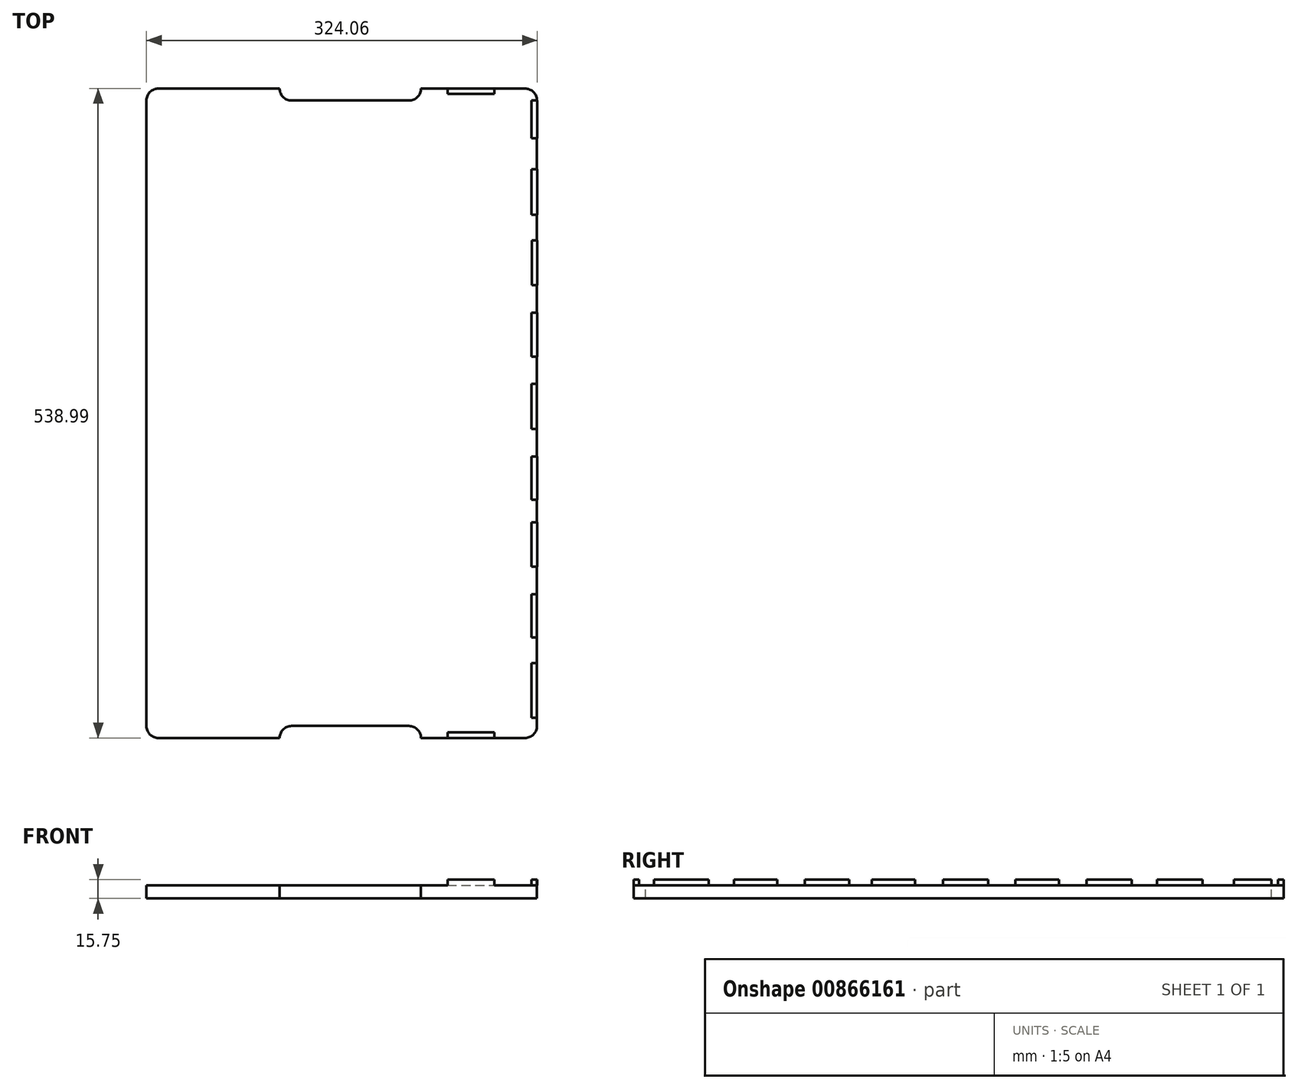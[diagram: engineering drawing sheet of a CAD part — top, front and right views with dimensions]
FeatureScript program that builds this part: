
annotation { "Feature Type Name" : "Feature", "Feature Type Description" : "" }
export const myFeature = defineFeature(function(context is Context, id is Id, definition is map)
    precondition{}
    {
        {
            var Q0;
            Q0=qCreatedBy(makeId("Top.planeOp"),FACE);
            var sketch = newSketch(context, id + "F0", { "sketchPlane" : qUnion([Q0])});
            skLineSegment(sketch, "E0.bottom", {"start": v(-151.16, 267.27) * mm, "end": v(-50.64, 267.27) * mm});
            skLineSegment(sketch, "E0.top", {"start": v(-151.16, -271.72) * mm, "end": v(152.88, -271.72) * mm});
            skLineSegment(sketch, "E0.left", {"start": v(-161.06, 257.36) * mm, "end": v(-161.06, -261.81) * mm});
            skLineSegment(sketch, "E0.right", {"start": v(162.79, 257.36) * mm, "end": v(162.79, -261.81) * mm});
            skPoint(sketch, "E1.visualSharp", {"position": v(-161.06, 267.27) * mm});
            skArc(sketch, "E1.filletArc", {"start": v(-151.16, 267.27) * mm, "mid": v(-158.16, 264.37) * mm, "end": v(-161.06, 257.36) * mm});
            skPoint(sketch, "E2.visualSharp", {"position": v(162.79, 267.27) * mm});
            skArc(sketch, "E2.filletArc", {"start": v(162.79, 257.36) * mm, "mid": v(159.89, 264.37) * mm, "end": v(152.88, 267.27) * mm});
            skPoint(sketch, "E3.visualSharp", {"position": v(162.79, -271.72) * mm});
            skArc(sketch, "E3.filletArc", {"start": v(152.88, -271.72) * mm, "mid": v(159.89, -268.82) * mm, "end": v(162.79, -261.81) * mm});
            skPoint(sketch, "E4.visualSharp", {"position": v(-161.06, -271.72) * mm});
            skArc(sketch, "E4.filletArc", {"start": v(-161.06, -261.81) * mm, "mid": v(-158.16, -268.82) * mm, "end": v(-151.16, -271.72) * mm});
            skPoint(sketch, "E5", {"position": v(-51.16, 267.27) * mm});
            skPoint(sketch, "E6", {"position": v(-41.25, 267.27) * mm});
            skPoint(sketch, "E7", {"position": v(66.6, 267.27) * mm});
            skPoint(sketch, "E8", {"position": v(56.7, 267.27) * mm});
            skLineSegment(sketch, "E9", {"start": v(-40.81, 267.27) * mm, "end": v(56.04, 267.27) * mm});
            skLineSegment(sketch, "E10", {"start": v(56.04, 267.27) * mm, "end": v(56.7, 267.27) * mm});
            skLineSegment(sketch, "E11", {"start": v(-41.25, 267.27) * mm, "end": v(-40.81, 267.27) * mm});
            skLineSegment(sketch, "E12.trimOffspring", {"start": v(66.6, 267.27) * mm, "end": v(152.88, 267.27) * mm});
            skLineSegment(sketch, "E13", {"start": v(-50.64, 267.27) * mm, "end": v(-40.81, 267.27) * mm});
            skLineSegment(sketch, "E14", {"start": v(56.7, 267.27) * mm, "end": v(66.6, 267.27) * mm});
            skPoint(sketch, "E15", {"position": v(-50.64, -271.72) * mm});
            skPoint(sketch, "E16", {"position": v(66.6, -271.72) * mm});
            skLineSegment(sketch, "E17.bottom", {"start": v(162.79, -254.96) * mm, "end": v(158.22, -254.96) * mm});
            skLineSegment(sketch, "E17.top", {"start": v(162.79, -209.49) * mm, "end": v(158.22, -209.49) * mm});
            skLineSegment(sketch, "E17.left", {"start": v(162.79, -254.96) * mm, "end": v(162.79, -209.49) * mm});
            skLineSegment(sketch, "E17.right", {"start": v(158.22, -254.96) * mm, "end": v(158.22, -209.49) * mm});
            skLineSegment(sketch, "E18.bottom", {"start": v(162.79, -188.4) * mm, "end": v(158.22, -188.4) * mm});
            skLineSegment(sketch, "E18.top", {"start": v(162.79, -152.6) * mm, "end": v(158.22, -152.6) * mm});
            skLineSegment(sketch, "E18.left", {"start": v(162.79, -188.4) * mm, "end": v(162.79, -152.6) * mm});
            skLineSegment(sketch, "E18.right", {"start": v(158.22, -188.4) * mm, "end": v(158.22, -152.6) * mm});
            skLineSegment(sketch, "E19.bottom", {"start": v(162.79, -129.73) * mm, "end": v(158.22, -129.73) * mm});
            skLineSegment(sketch, "E19.top", {"start": v(162.79, -92.9) * mm, "end": v(158.22, -92.9) * mm});
            skLineSegment(sketch, "E19.left", {"start": v(162.79, -129.73) * mm, "end": v(162.79, -92.9) * mm});
            skLineSegment(sketch, "E19.right", {"start": v(158.22, -129.73) * mm, "end": v(158.22, -92.9) * mm});
            skLineSegment(sketch, "E20.bottom", {"start": v(162.79, -74.1) * mm, "end": v(158.22, -74.1) * mm});
            skLineSegment(sketch, "E20.top", {"start": v(162.79, -38.3) * mm, "end": v(158.22, -38.3) * mm});
            skLineSegment(sketch, "E20.left", {"start": v(162.79, -74.1) * mm, "end": v(162.79, -38.3) * mm});
            skLineSegment(sketch, "E20.right", {"start": v(158.22, -74.1) * mm, "end": v(158.22, -38.3) * mm});
            skLineSegment(sketch, "E21.bottom", {"start": v(162.79, -15.18) * mm, "end": v(158.22, -15.18) * mm});
            skLineSegment(sketch, "E21.top", {"start": v(162.79, 22.16) * mm, "end": v(158.22, 22.16) * mm});
            skLineSegment(sketch, "E21.left", {"start": v(162.79, -15.18) * mm, "end": v(162.79, 22.16) * mm});
            skLineSegment(sketch, "E21.right", {"start": v(158.22, -15.18) * mm, "end": v(158.22, 22.16) * mm});
            skLineSegment(sketch, "E22.bottom", {"start": v(162.79, 44.76) * mm, "end": v(158.22, 44.76) * mm});
            skLineSegment(sketch, "E22.top", {"start": v(162.79, 81.09) * mm, "end": v(158.22, 81.09) * mm});
            skLineSegment(sketch, "E22.left", {"start": v(162.79, 44.76) * mm, "end": v(162.79, 81.09) * mm});
            skLineSegment(sketch, "E22.right", {"start": v(158.22, 44.76) * mm, "end": v(158.22, 81.09) * mm});
            skLineSegment(sketch, "E23.bottom", {"start": v(162.79, 103.95) * mm, "end": v(158.22, 103.95) * mm});
            skLineSegment(sketch, "E23.top", {"start": v(162.79, 141.28) * mm, "end": v(158.22, 141.28) * mm});
            skLineSegment(sketch, "E23.left", {"start": v(162.79, 103.95) * mm, "end": v(162.79, 141.28) * mm});
            skLineSegment(sketch, "E23.right", {"start": v(158.22, 103.95) * mm, "end": v(158.22, 141.28) * mm});
            skLineSegment(sketch, "E24.bottom", {"start": v(162.79, 162.37) * mm, "end": v(158.22, 162.37) * mm});
            skLineSegment(sketch, "E24.top", {"start": v(162.79, 200.21) * mm, "end": v(158.22, 200.21) * mm});
            skLineSegment(sketch, "E24.left", {"start": v(162.79, 162.37) * mm, "end": v(162.79, 200.21) * mm});
            skLineSegment(sketch, "E24.right", {"start": v(158.22, 162.37) * mm, "end": v(158.22, 200.21) * mm});
            skLineSegment(sketch, "E25.bottom", {"start": v(162.79, 226.12) * mm, "end": v(158.22, 226.12) * mm});
            skLineSegment(sketch, "E25.top", {"start": v(162.79, 257.36) * mm, "end": v(158.22, 257.36) * mm});
            skLineSegment(sketch, "E25.left", {"start": v(162.79, 226.12) * mm, "end": v(162.79, 257.36) * mm});
            skLineSegment(sketch, "E25.right", {"start": v(158.22, 226.12) * mm, "end": v(158.22, 257.36) * mm});
            skSolve(sketch);
        }
        {
            var Q0;
            Q0 = qSketchRegion(id + "F0", true);
            extrude(context, id + "F1", {"entities" : qUnion([Q0]), "depth" : 10.92 * mm, "offsetDistance" : 25.4 * mm});
        }
        {
            var Q0;
            Q0=makeQuery(id+"F1.opExtrude","CAP_FACE",FACE,{"disambiguationData":[OSD([sQuery(id+"F0.wireOp",EDGE,"E0.bottom"),sQuery(id+"F0.wireOp",EDGE,"E0.top"),sQuery(id+"F0.wireOp",EDGE,"E0.left"),sQuery(id+"F0.wireOp",EDGE,"E0.right"),sQuery(id+"F0.wireOp",EDGE,"E1.filletArc"),sQuery(id+"F0.wireOp",EDGE,"E2.filletArc"),sQuery(id+"F0.wireOp",EDGE,"E3.filletArc"),sQuery(id+"F0.wireOp",EDGE,"E4.filletArc"),sQuery(id+"F0.wireOp",EDGE,"E9"),sQuery(id+"F0.wireOp",EDGE,"E10"),sQuery(id+"F0.wireOp",EDGE,"E12.trimOffspring"),sQuery(id+"F0.wireOp",EDGE,"E13"),sQuery(id+"F0.wireOp",EDGE,"E14")])],"isStart":false});
            var sketch = newSketch(context, id + "F2", { "sketchPlane" : qUnion([Q0])});
            skLineSegment(sketch, "E26.bottom", {"start": v(-50.65, 267.27) * mm, "end": v(66.6, 267.27) * mm});
            skLineSegment(sketch, "E26.top", {"start": v(-40.75, 257.36) * mm, "end": v(56.69, 257.36) * mm});
            skLineSegment(sketch, "E26.left", {"start": v(-50.65, 267.27) * mm, "end": v(-50.65, 267.27) * mm});
            skLineSegment(sketch, "E26.right", {"start": v(66.6, 267.27) * mm, "end": v(66.6, 267.27) * mm});
            skPoint(sketch, "E27.visualSharp", {"position": v(-50.65, 257.36) * mm});
            skArc(sketch, "E27.filletArc", {"start": v(-50.65, 267.27) * mm, "mid": v(-47.75, 260.26) * mm, "end": v(-40.75, 257.36) * mm});
            skPoint(sketch, "E28.visualSharp", {"position": v(66.6, 257.36) * mm});
            skArc(sketch, "E28.filletArc", {"start": v(56.69, 257.36) * mm, "mid": v(63.7, 260.26) * mm, "end": v(66.6, 267.27) * mm});
            skSolve(sketch);
        }
        {
            var Q0;
            Q0 = qSketchRegion(id + "F2", true);
            extrude(context, id + "F3", {"entities" : qUnion([Q0]), "operationType" : NewBodyOperationType.REMOVE, "endBound" : BoundingType.THROUGH_ALL, "oppositeDirection" : true, "depth" : 10.92 * mm, "offsetDistance" : 25.4 * mm});
        }
        {
            var Q0;
            Q0=makeQuery(id+"F2.imprint","IMPRINT",FACE,{"disambiguationData":[TD([[makeQuery(id+"F2.imprint","IMPRINT",EDGE,{"derivedFrom":sQuery(id+"F2.wireOp",EDGE,"E26.top")}),-1.0]])]});
            var sketch = newSketch(context, id + "F4", { "sketchPlane" : qUnion([Q0])});
            skLineSegment(sketch, "E29.bottom", {"start": v(-40.74, -261.81) * mm, "end": v(56.7, -261.81) * mm});
            skLineSegment(sketch, "E29.top", {"start": v(-50.64, -271.74) * mm, "end": v(66.6, -271.74) * mm});
            skLineSegment(sketch, "E29.left", {"start": v(-50.64, -271.72) * mm, "end": v(-50.64, -271.74) * mm});
            skLineSegment(sketch, "E29.right", {"start": v(66.6, -271.72) * mm, "end": v(66.6, -271.74) * mm});
            skPoint(sketch, "E30.visualSharp", {"position": v(-50.64, -261.81) * mm});
            skArc(sketch, "E30.filletArc", {"start": v(-40.74, -261.81) * mm, "mid": v(-47.74, -264.71) * mm, "end": v(-50.64, -271.72) * mm});
            skPoint(sketch, "E31.visualSharp", {"position": v(66.6, -261.81) * mm});
            skArc(sketch, "E31.filletArc", {"start": v(66.6, -271.72) * mm, "mid": v(63.7, -264.71) * mm, "end": v(56.7, -261.81) * mm});
            skSolve(sketch);
        }
        {
            var Q0;
            Q0 = qSketchRegion(id + "F4", true);
            extrude(context, id + "F5", {"entities" : qUnion([Q0]), "operationType" : NewBodyOperationType.REMOVE, "endBound" : BoundingType.THROUGH_ALL, "oppositeDirection" : true, "depth" : 10.92 * mm, "offsetDistance" : 25.4 * mm});
        }
        {
            var Q0;
            Q0=makeQuery(id+"F2.imprint","IMPRINT",FACE,{"disambiguationData":[TD([[makeQuery(id+"F2.imprint","IMPRINT",EDGE,{"derivedFrom":sQuery(id+"F2.wireOp",EDGE,"E26.top")}),-1.0]])]});
            var sketch = newSketch(context, id + "F6", { "sketchPlane" : qUnion([Q0])});
            skLineSegment(sketch, "E32.bottom", {"start": v(158.23, -209.49) * mm, "end": v(162.8, -209.49) * mm});
            skLineSegment(sketch, "E32.top", {"start": v(158.23, -254.96) * mm, "end": v(162.8, -254.96) * mm});
            skLineSegment(sketch, "E32.left", {"start": v(158.23, -209.49) * mm, "end": v(158.23, -254.96) * mm});
            skLineSegment(sketch, "E32.right", {"start": v(162.8, -209.49) * mm, "end": v(162.8, -254.96) * mm});
            skSolve(sketch);
        }
        {
            var Q0;
            Q0 = qSketchRegion(id + "F6", true);
            extrude(context, id + "F7", {"entities" : qUnion([Q0]), "operationType" : NewBodyOperationType.ADD, "depth" : 4.83 * mm, "offsetDistance" : 25.4 * mm});
        }
        {
            var Q0;
            Q0=makeQuery(id+"F2.imprint","IMPRINT",FACE,{"disambiguationData":[TD([[makeQuery(id+"F2.imprint","IMPRINT",EDGE,{"derivedFrom":sQuery(id+"F2.wireOp",EDGE,"E26.top")}),-1.0]])]});
            var sketch = newSketch(context, id + "F8", { "sketchPlane" : qUnion([Q0])});
            skLineSegment(sketch, "E33.bottom", {"start": v(158.13, -152.6) * mm, "end": v(162.7, -152.6) * mm});
            skLineSegment(sketch, "E33.top", {"start": v(158.13, -188.4) * mm, "end": v(162.7, -188.4) * mm});
            skLineSegment(sketch, "E33.left", {"start": v(158.13, -152.6) * mm, "end": v(158.13, -188.4) * mm});
            skLineSegment(sketch, "E33.right", {"start": v(162.7, -152.6) * mm, "end": v(162.7, -188.4) * mm});
            skSolve(sketch);
        }
        {
            var Q0;
            Q0 = qSketchRegion(id + "F8", true);
            extrude(context, id + "F9", {"entities" : qUnion([Q0]), "operationType" : NewBodyOperationType.ADD, "depth" : 4.83 * mm, "offsetDistance" : 25.4 * mm});
        }
        {
            var Q0;
            Q0=makeQuery(id+"F2.imprint","IMPRINT",FACE,{"disambiguationData":[TD([[makeQuery(id+"F2.imprint","IMPRINT",EDGE,{"derivedFrom":sQuery(id+"F2.wireOp",EDGE,"E26.top")}),-1.0]])]});
            var sketch = newSketch(context, id + "F10", { "sketchPlane" : qUnion([Q0])});
            skLineSegment(sketch, "E34.bottom", {"start": v(158.29, -92.9) * mm, "end": v(162.86, -92.9) * mm});
            skLineSegment(sketch, "E34.top", {"start": v(158.29, -129.73) * mm, "end": v(162.86, -129.73) * mm});
            skLineSegment(sketch, "E34.left", {"start": v(158.29, -92.9) * mm, "end": v(158.29, -129.73) * mm});
            skLineSegment(sketch, "E34.right", {"start": v(162.86, -92.9) * mm, "end": v(162.86, -129.73) * mm});
            skSolve(sketch);
        }
        {
            var Q0;
            Q0 = qSketchRegion(id + "F10", true);
            extrude(context, id + "F11", {"entities" : qUnion([Q0]), "operationType" : NewBodyOperationType.ADD, "depth" : 4.83 * mm, "offsetDistance" : 25.4 * mm});
        }
        {
            var Q0;
            Q0=makeQuery(id+"F2.imprint","IMPRINT",FACE,{"disambiguationData":[TD([[makeQuery(id+"F2.imprint","IMPRINT",EDGE,{"derivedFrom":sQuery(id+"F2.wireOp",EDGE,"E26.top")}),-1.0]])]});
            var sketch = newSketch(context, id + "F12", { "sketchPlane" : qUnion([Q0])});
            skLineSegment(sketch, "E35.bottom", {"start": v(158.29, -38.3) * mm, "end": v(162.86, -38.3) * mm});
            skLineSegment(sketch, "E35.top", {"start": v(158.29, -74.1) * mm, "end": v(162.86, -74.1) * mm});
            skLineSegment(sketch, "E35.left", {"start": v(158.29, -38.3) * mm, "end": v(158.29, -74.1) * mm});
            skLineSegment(sketch, "E35.right", {"start": v(162.86, -38.3) * mm, "end": v(162.86, -74.1) * mm});
            skSolve(sketch);
        }
        {
            var Q0;
            Q0 = qSketchRegion(id + "F12", true);
            extrude(context, id + "F13", {"entities" : qUnion([Q0]), "operationType" : NewBodyOperationType.ADD, "depth" : 4.83 * mm, "offsetDistance" : 25.4 * mm});
        }
        {
            var Q0;
            Q0=makeQuery(id+"F2.imprint","IMPRINT",FACE,{"disambiguationData":[TD([[makeQuery(id+"F2.imprint","IMPRINT",EDGE,{"derivedFrom":sQuery(id+"F2.wireOp",EDGE,"E26.top")}),-1.0]])]});
            var sketch = newSketch(context, id + "F14", { "sketchPlane" : qUnion([Q0])});
            skLineSegment(sketch, "E36.bottom", {"start": v(158.11, 22.16) * mm, "end": v(162.68, 22.16) * mm});
            skLineSegment(sketch, "E36.top", {"start": v(158.11, -15.18) * mm, "end": v(162.68, -15.18) * mm});
            skLineSegment(sketch, "E36.left", {"start": v(158.11, 22.16) * mm, "end": v(158.11, -15.18) * mm});
            skLineSegment(sketch, "E36.right", {"start": v(162.68, 22.16) * mm, "end": v(162.68, -15.18) * mm});
            skSolve(sketch);
        }
        {
            var Q0;
            Q0 = qSketchRegion(id + "F14", true);
            extrude(context, id + "F15", {"entities" : qUnion([Q0]), "operationType" : NewBodyOperationType.ADD, "depth" : 4.83 * mm, "offsetDistance" : 25.4 * mm});
        }
        {
            var Q0;
            Q0=makeQuery(id+"F2.imprint","IMPRINT",FACE,{"disambiguationData":[TD([[makeQuery(id+"F2.imprint","IMPRINT",EDGE,{"derivedFrom":sQuery(id+"F2.wireOp",EDGE,"E26.top")}),-1.0]])]});
            var sketch = newSketch(context, id + "F16", { "sketchPlane" : qUnion([Q0])});
            skLineSegment(sketch, "E37.bottom", {"start": v(158.38, 81.09) * mm, "end": v(162.95, 81.09) * mm});
            skLineSegment(sketch, "E37.top", {"start": v(158.38, 44.76) * mm, "end": v(162.95, 44.76) * mm});
            skLineSegment(sketch, "E37.left", {"start": v(158.38, 81.09) * mm, "end": v(158.38, 44.76) * mm});
            skLineSegment(sketch, "E37.right", {"start": v(162.95, 81.09) * mm, "end": v(162.95, 44.76) * mm});
            skSolve(sketch);
        }
        {
            var Q0;
            Q0 = qSketchRegion(id + "F16", true);
            extrude(context, id + "F17", {"entities" : qUnion([Q0]), "operationType" : NewBodyOperationType.ADD, "depth" : 4.83 * mm, "offsetDistance" : 25.4 * mm});
        }
        {
            var Q0;
            Q0=makeQuery(id+"F2.imprint","IMPRINT",FACE,{"disambiguationData":[TD([[makeQuery(id+"F2.imprint","IMPRINT",EDGE,{"derivedFrom":sQuery(id+"F2.wireOp",EDGE,"E26.top")}),-1.0]])]});
            var sketch = newSketch(context, id + "F18", { "sketchPlane" : qUnion([Q0])});
            skLineSegment(sketch, "E38.bottom", {"start": v(158.43, 141.28) * mm, "end": v(163, 141.28) * mm});
            skLineSegment(sketch, "E38.top", {"start": v(158.43, 103.95) * mm, "end": v(163, 103.95) * mm});
            skLineSegment(sketch, "E38.left", {"start": v(158.43, 141.28) * mm, "end": v(158.43, 103.95) * mm});
            skLineSegment(sketch, "E38.right", {"start": v(163, 141.28) * mm, "end": v(163, 103.95) * mm});
            skSolve(sketch);
        }
        {
            var Q0;
            Q0 = qSketchRegion(id + "F18", true);
            extrude(context, id + "F19", {"entities" : qUnion([Q0]), "operationType" : NewBodyOperationType.ADD, "depth" : 4.83 * mm, "offsetDistance" : 25.4 * mm});
        }
        {
            var Q0;
            Q0=makeQuery(id+"F2.imprint","IMPRINT",FACE,{"disambiguationData":[TD([[makeQuery(id+"F2.imprint","IMPRINT",EDGE,{"derivedFrom":sQuery(id+"F2.wireOp",EDGE,"E26.top")}),-1.0]])]});
            var sketch = newSketch(context, id + "F20", { "sketchPlane" : qUnion([Q0])});
            skLineSegment(sketch, "E39.bottom", {"start": v(158.28, 200.21) * mm, "end": v(162.85, 200.21) * mm});
            skLineSegment(sketch, "E39.top", {"start": v(158.28, 162.37) * mm, "end": v(162.85, 162.37) * mm});
            skLineSegment(sketch, "E39.left", {"start": v(158.28, 200.21) * mm, "end": v(158.28, 162.37) * mm});
            skLineSegment(sketch, "E39.right", {"start": v(162.85, 200.21) * mm, "end": v(162.85, 162.37) * mm});
            skSolve(sketch);
        }
        {
            var Q0;
            Q0 = qSketchRegion(id + "F20", true);
            extrude(context, id + "F21", {"entities" : qUnion([Q0]), "operationType" : NewBodyOperationType.ADD, "depth" : 4.83 * mm, "offsetDistance" : 25.4 * mm});
        }
        {
            var Q0;
            Q0=makeQuery(id+"F2.imprint","IMPRINT",FACE,{"disambiguationData":[TD([[makeQuery(id+"F2.imprint","IMPRINT",EDGE,{"derivedFrom":sQuery(id+"F2.wireOp",EDGE,"E26.top")}),-1.0]])]});
            var sketch = newSketch(context, id + "F22", { "sketchPlane" : qUnion([Q0])});
            skLineSegment(sketch, "E40.bottom", {"start": v(158.28, 257.36) * mm, "end": v(162.85, 257.36) * mm});
            skLineSegment(sketch, "E40.top", {"start": v(158.28, 226.12) * mm, "end": v(162.85, 226.12) * mm});
            skLineSegment(sketch, "E40.left", {"start": v(158.28, 257.36) * mm, "end": v(158.28, 226.12) * mm});
            skLineSegment(sketch, "E40.right", {"start": v(162.85, 257.36) * mm, "end": v(162.85, 226.12) * mm});
            skSolve(sketch);
        }
        {
            var Q0;
            Q0 = qSketchRegion(id + "F22", true);
            extrude(context, id + "F23", {"entities" : qUnion([Q0]), "operationType" : NewBodyOperationType.ADD, "depth" : 4.83 * mm, "offsetDistance" : 25.4 * mm});
        }
        {
            var Q0;
            Q0=makeQuery(id+"F2.imprint","IMPRINT",FACE,{"disambiguationData":[TD([[makeQuery(id+"F2.imprint","IMPRINT",EDGE,{"derivedFrom":sQuery(id+"F2.wireOp",EDGE,"E26.top")}),-1.0]])]});
            var sketch = newSketch(context, id + "F24", { "sketchPlane" : qUnion([Q0])});
            skLineSegment(sketch, "E41.bottom", {"start": v(88.62, 267.27) * mm, "end": v(127.48, 267.27) * mm});
            skLineSegment(sketch, "E41.top", {"start": v(88.62, 262.7) * mm, "end": v(127.48, 262.7) * mm});
            skLineSegment(sketch, "E41.left", {"start": v(88.62, 267.27) * mm, "end": v(88.62, 262.7) * mm});
            skLineSegment(sketch, "E41.right", {"start": v(127.48, 267.27) * mm, "end": v(127.48, 262.7) * mm});
            skSolve(sketch);
        }
        {
            var Q0;
            Q0 = qSketchRegion(id + "F24", true);
            extrude(context, id + "F25", {"entities" : qUnion([Q0]), "operationType" : NewBodyOperationType.ADD, "depth" : 4.83 * mm, "offsetDistance" : 25.4 * mm});
        }
        {
            var Q0;
            Q0=makeQuery(id+"F2.imprint","IMPRINT",FACE,{"disambiguationData":[TD([[makeQuery(id+"F2.imprint","IMPRINT",EDGE,{"derivedFrom":sQuery(id+"F2.wireOp",EDGE,"E26.top")}),-1.0]])]});
            var sketch = newSketch(context, id + "F26", { "sketchPlane" : qUnion([Q0])});
            skLineSegment(sketch, "E42.bottom", {"start": v(88.62, -271.72) * mm, "end": v(127.48, -271.72) * mm});
            skLineSegment(sketch, "E42.top", {"start": v(88.62, -267.15) * mm, "end": v(127.48, -267.15) * mm});
            skLineSegment(sketch, "E42.left", {"start": v(88.62, -271.72) * mm, "end": v(88.62, -267.15) * mm});
            skLineSegment(sketch, "E42.right", {"start": v(127.48, -271.72) * mm, "end": v(127.48, -267.15) * mm});
            skSolve(sketch);
        }
        {
            var Q0;
            Q0 = qSketchRegion(id + "F26", true);
            extrude(context, id + "F27", {"entities" : qUnion([Q0]), "operationType" : NewBodyOperationType.ADD, "depth" : 4.83 * mm, "offsetDistance" : 25.4 * mm});
        }
    });
